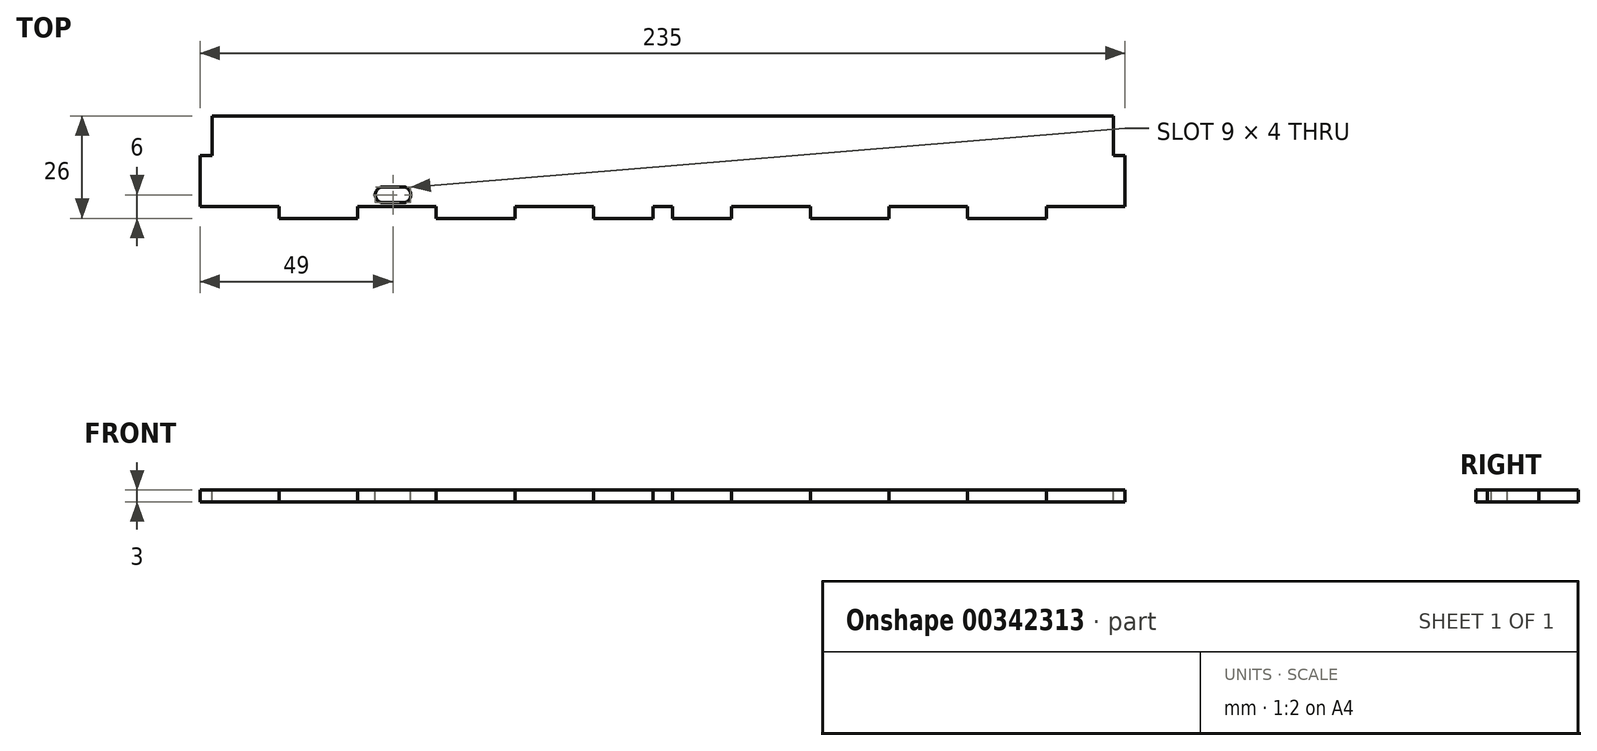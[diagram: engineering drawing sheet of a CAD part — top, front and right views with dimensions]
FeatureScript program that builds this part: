
annotation { "Feature Type Name" : "Feature", "Feature Type Description" : "" }
export const myFeature = defineFeature(function(context is Context, id is Id, definition is map)
    precondition{}
    {
        {
            var Q0;
            Q0=qCreatedBy(makeId("Top.planeOp"),FACE);
            var sketch = newSketch(context, id + "F0", { "sketchPlane" : qUnion([Q0])});
            skLineSegment(sketch, "E0.top", {"start": v(-17, 26) * mm, "end": v(212, 26) * mm});
            skLineSegment(sketch, "E1.top", {"start": v(-20, 3) * mm, "end": v(0, 3) * mm});
            skLineSegment(sketch, "E1.right", {"start": v(0, 0) * mm, "end": v(0, 3) * mm});
            skLineSegment(sketch, "E2.top", {"start": v(215, 3) * mm, "end": v(195, 3) * mm});
            skLineSegment(sketch, "E2.right", {"start": v(195, 0) * mm, "end": v(195, 3) * mm});
            skLineSegment(sketch, "E3", {"start": v(0, 0) * mm, "end": v(20, 0) * mm});
            skLineSegment(sketch, "E4", {"start": v(20, 0) * mm, "end": v(20, 3) * mm});
            skLineSegment(sketch, "E5", {"start": v(20, 3) * mm, "end": v(40, 3) * mm});
            skLineSegment(sketch, "E6", {"start": v(40, 3) * mm, "end": v(40, 0) * mm});
            skLineSegment(sketch, "E7", {"start": v(40, 0) * mm, "end": v(60, 0) * mm});
            skLineSegment(sketch, "E8", {"start": v(60, 0) * mm, "end": v(60, 3) * mm});
            skLineSegment(sketch, "E9", {"start": v(60, 3) * mm, "end": v(80, 3) * mm});
            skLineSegment(sketch, "E10", {"start": v(80, 3) * mm, "end": v(80, 0) * mm});
            skLineSegment(sketch, "E11", {"start": v(115, 0) * mm, "end": v(115, 3) * mm});
            skLineSegment(sketch, "E12", {"start": v(115, 3) * mm, "end": v(135, 3) * mm});
            skLineSegment(sketch, "E13", {"start": v(135, 3) * mm, "end": v(135, 0) * mm});
            skLineSegment(sketch, "E14", {"start": v(135, 0) * mm, "end": v(155, 0) * mm});
            skLineSegment(sketch, "E15", {"start": v(155, 0) * mm, "end": v(155, 3) * mm});
            skLineSegment(sketch, "E16", {"start": v(155, 3) * mm, "end": v(175, 3) * mm});
            skLineSegment(sketch, "E17", {"start": v(175, 3) * mm, "end": v(175, 0) * mm});
            skLineSegment(sketch, "E18", {"start": v(175, 0) * mm, "end": v(195, 0) * mm});
            skLineSegment(sketch, "E19", {"start": v(215, 16) * mm, "end": v(212, 16) * mm});
            skLineSegment(sketch, "E20", {"start": v(212, 16) * mm, "end": v(212, 26) * mm});
            skLineSegment(sketch, "E21", {"start": v(215, 16) * mm, "end": v(215, 3) * mm});
            skLineSegment(sketch, "E22", {"start": v(-20, 3) * mm, "end": v(-20, 16) * mm});
            skLineSegment(sketch, "E23", {"start": v(-20, 16) * mm, "end": v(-17, 16) * mm});
            skLineSegment(sketch, "E24", {"start": v(-17, 16) * mm, "end": v(-17, 26) * mm});
            skLineSegment(sketch, "E25", {"start": v(80, 0) * mm, "end": v(95, 0) * mm});
            skLineSegment(sketch, "E26", {"start": v(95, 0) * mm, "end": v(95, 3) * mm});
            skLineSegment(sketch, "E27", {"start": v(115, 0) * mm, "end": v(100, 0) * mm});
            skLineSegment(sketch, "E28", {"start": v(100, 0) * mm, "end": v(100, 3) * mm});
            skLineSegment(sketch, "E29", {"start": v(95, 3) * mm, "end": v(100, 3) * mm});
            skLineSegment(sketch, "E30", {"start": v(97.5, 26) * mm, "end": v(97.5, 3) * mm});
            skLineSegment(sketch, "E31.bottom", {"start": v(26.5, 8) * mm, "end": v(31.5, 8) * mm});
            skLineSegment(sketch, "E31.top", {"start": v(26.5, 4) * mm, "end": v(31.5, 4) * mm});
            skLineSegment(sketch, "E31.left", {"start": v(24.5, 6) * mm, "end": v(24.5, 6) * mm});
            skLineSegment(sketch, "E31.right", {"start": v(33.5, 6) * mm, "end": v(33.5, 6) * mm});
            skLineSegment(sketch, "E32", {"start": v(29, 8) * mm, "end": v(29, 4) * mm, "construction": true});
            skLineSegment(sketch, "E33", {"start": v(29, 6) * mm, "end": v(24.5, 6) * mm, "construction": true});
            skPoint(sketch, "E34.visualSharp", {"position": v(33.5, 8) * mm});
            skArc(sketch, "E34.filletArc", {"start": v(33.5, 6) * mm, "mid": v(32.91, 7.41) * mm, "end": v(31.5, 8) * mm});
            skPoint(sketch, "E35.visualSharp", {"position": v(24.5, 8) * mm});
            skArc(sketch, "E35.filletArc", {"start": v(26.5, 8) * mm, "mid": v(25.09, 7.41) * mm, "end": v(24.5, 6) * mm});
            skPoint(sketch, "E36.visualSharp", {"position": v(24.5, 4) * mm});
            skArc(sketch, "E36.filletArc", {"start": v(24.5, 6) * mm, "mid": v(25.09, 4.59) * mm, "end": v(26.5, 4) * mm});
            skPoint(sketch, "E37.visualSharp", {"position": v(33.5, 4) * mm});
            skArc(sketch, "E37.filletArc", {"start": v(31.5, 4) * mm, "mid": v(32.91, 4.59) * mm, "end": v(33.5, 6) * mm});
            skSolve(sketch);
        }
        {
            var Q0;
            Q0 = qSketchRegion(id + "F0", true);
            extrude(context, id + "F1", {"entities" : qUnion([Q0]), "oppositeDirection" : true, "offsetDistance" : 25 * mm, "depth" : 3 * mm});
        }
    });
